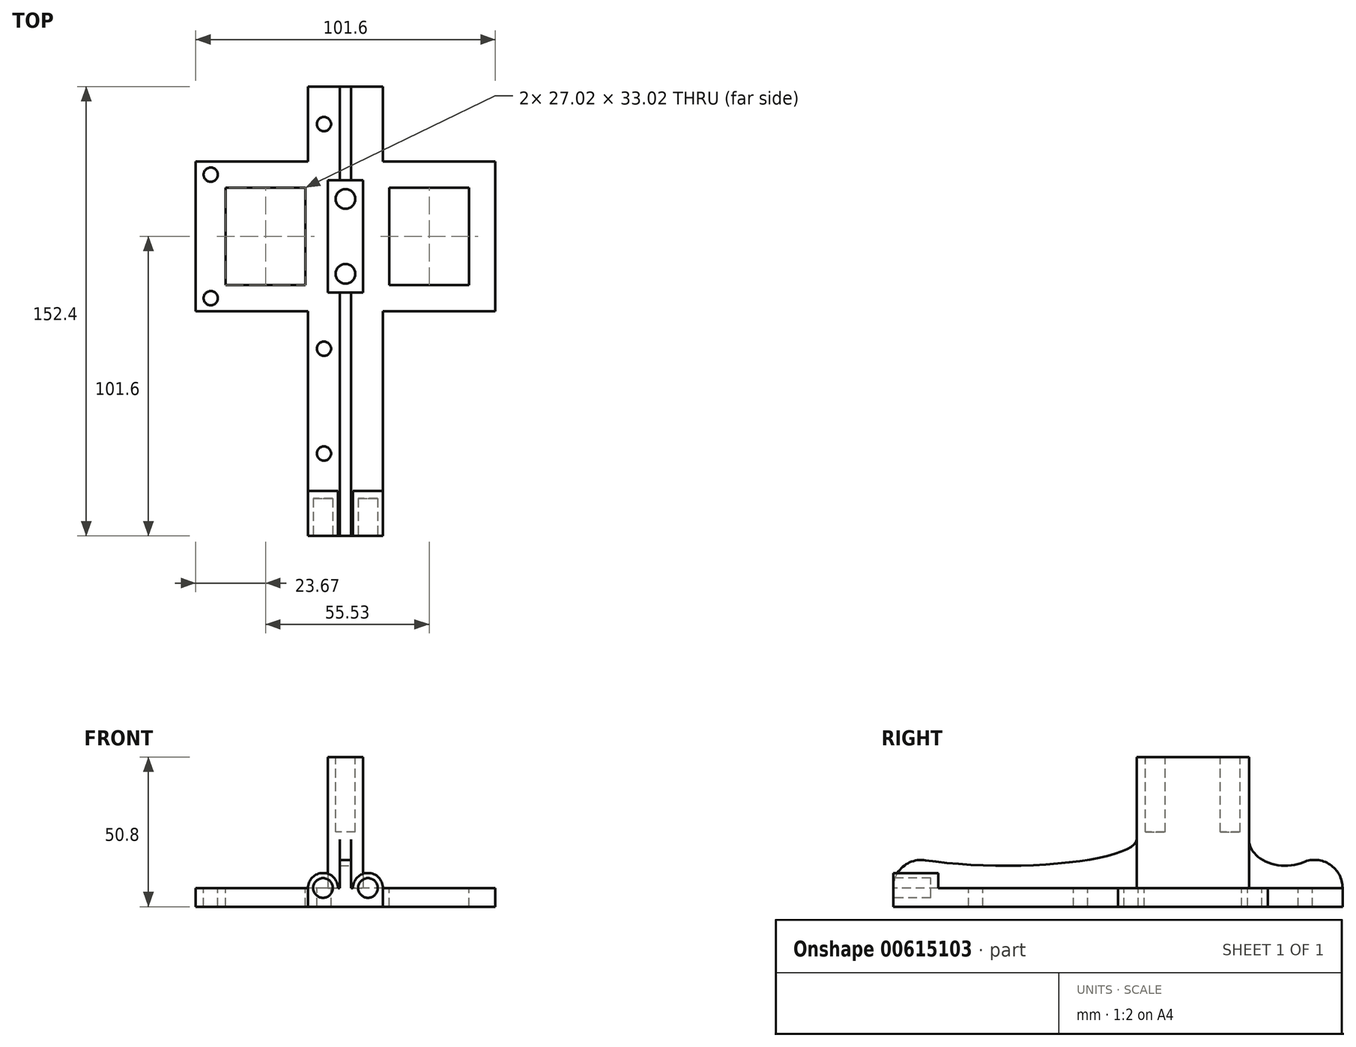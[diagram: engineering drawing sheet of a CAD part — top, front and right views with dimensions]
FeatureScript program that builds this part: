
annotation { "Feature Type Name" : "Feature", "Feature Type Description" : "" }
export const myFeature = defineFeature(function(context is Context, id is Id, definition is map)
    precondition{}
    {
        {
            var Q0;
            Q0=qCreatedBy(makeId("Top.planeOp"),FACE);
            var sketch = newSketch(context, id + "F0", { "sketchPlane" : qUnion([Q0])});
            skLineSegment(sketch, "E0.bottom", {"start": v(-6, 19.05) * mm, "end": v(6, 19.05) * mm});
            skLineSegment(sketch, "E0.top", {"start": v(-6, -19.05) * mm, "end": v(6, -19.05) * mm});
            skLineSegment(sketch, "E0.left", {"start": v(-6, 19.05) * mm, "end": v(-6, -19.05) * mm});
            skLineSegment(sketch, "E0.right", {"start": v(6, 19.05) * mm, "end": v(6, -19.05) * mm});
            skPoint(sketch, "E0.middle", {"position": v(0, 0) * mm});
            skSolve(sketch);
        }
        {
            var Q0;
            Q0 = qSketchRegion(id + "F0", true);
            extrude(context, id + "F1", {"entities" : qUnion([Q0]), "depth" : 50.8 * mm, "offsetDistance" : 25.4 * mm});
        }
        {
            var Q0;
            Q0=makeQuery(id+"F1.opExtrude","CAP_FACE",FACE,{"disambiguationData":[OSD([sQuery(id+"F0.wireOp",EDGE,"E0.bottom"),sQuery(id+"F0.wireOp",EDGE,"E0.top"),sQuery(id+"F0.wireOp",EDGE,"E0.left"),sQuery(id+"F0.wireOp",EDGE,"E0.right")])],"isStart":false});
            var sketch = newSketch(context, id + "F2", { "sketchPlane" : qUnion([Q0])});
            skCircle(sketch, "E1", {"center": v(0, 12.7) * mm, "radius": 3.33 * mm});
            skCircle(sketch, "E2", {"center": v(0, -12.7) * mm, "radius": 3.33 * mm});
            skSolve(sketch);
        }
        {
            var Q0;
            Q0 = qSketchRegion(id + "F2", true);
            extrude(context, id + "F3", {"entities" : qUnion([Q0]), "operationType" : NewBodyOperationType.REMOVE, "oppositeDirection" : true, "depth" : 25.4 * mm, "offsetDistance" : 25.4 * mm});
        }
        {
            var Q0;
            Q0=makeQuery(id+"F1.opExtrude","CAP_FACE",FACE,{"disambiguationData":[OSD([sQuery(id+"F0.wireOp",EDGE,"E0.bottom"),sQuery(id+"F0.wireOp",EDGE,"E0.top"),sQuery(id+"F0.wireOp",EDGE,"E0.left"),sQuery(id+"F0.wireOp",EDGE,"E0.right")])],"isStart":true});
            var sketch = newSketch(context, id + "F4", { "sketchPlane" : qUnion([Q0])});
            skLineSegment(sketch, "E3.0.0", {"start": v(-6, 19.05) * mm, "end": v(-6, -19.05) * mm});
            skLineSegment(sketch, "E3.0.1", {"start": v(-6, -19.05) * mm, "end": v(6, -19.05) * mm});
            skLineSegment(sketch, "E3.0.2", {"start": v(6, -19.05) * mm, "end": v(6, 19.05) * mm});
            skLineSegment(sketch, "E3.0.3", {"start": v(6, 19.05) * mm, "end": v(-6, 19.05) * mm});
            skLineSegment(sketch, "E4.bottom", {"start": v(12.7, 101.6) * mm, "end": v(-12.7, 101.6) * mm});
            skLineSegment(sketch, "E4.top", {"start": v(12.7, -50.8) * mm, "end": v(-12.7, -50.8) * mm});
            skLineSegment(sketch, "E4.left", {"start": v(12.7, 101.6) * mm, "end": v(12.7, -50.8) * mm});
            skLineSegment(sketch, "E4.right", {"start": v(-12.7, 101.6) * mm, "end": v(-12.7, -50.8) * mm});
            skPoint(sketch, "E4.middle", {"position": v(0, 25.4) * mm});
            skLineSegment(sketch, "E5.bottom", {"start": v(-50.8, 25.4) * mm, "end": v(50.8, 25.4) * mm});
            skLineSegment(sketch, "E5.top", {"start": v(-50.8, -25.4) * mm, "end": v(50.8, -25.4) * mm});
            skLineSegment(sketch, "E5.left", {"start": v(-50.8, 25.4) * mm, "end": v(-50.8, -25.4) * mm});
            skLineSegment(sketch, "E5.right", {"start": v(50.8, 25.4) * mm, "end": v(50.8, -25.4) * mm});
            skPoint(sketch, "E5.middle", {"position": v(0, 0) * mm});
            skLineSegment(sketch, "E6", {"start": v(0, 0) * mm, "end": v(0, 95.25) * mm, "construction": true});
            skSolve(sketch);
        }
        {
            var Q0;
            Q0 = qSketchRegion(id + "F4", true);
            extrude(context, id + "F5", {"entities" : qUnion([Q0]), "operationType" : NewBodyOperationType.ADD, "oppositeDirection" : true, "depth" : 6.35 * mm, "offsetDistance" : 25.4 * mm});
        }
        {
            var Q0;
            Q0=qCreatedBy(makeId("Right.planeOp"),FACE);
            var sketch = newSketch(context, id + "F6", { "sketchPlane" : qUnion([Q0])});
            skLineSegment(sketch, "E7.0", {"start": v(-19.05, 50.8) * mm, "end": v(-19.05, 6.35) * mm});
            skLineSegment(sketch, "E8.0", {"start": v(-101.6, 6.35) * mm, "end": v(-25.4, 6.35) * mm});
            skLineSegment(sketch, "E9.0", {"start": v(-25.4, 6.35) * mm, "end": v(25.4, 6.35) * mm});
            skEllipse(sketch, "E10", {"center": v(-63.5, 22.86) * mm, "majorRadius": 44.45 * mm, "minorRadius": 8.96 * mm, "majorAxis": v(1, 0), "construction": true});
            skCircle(sketch, "E11", {"center": v(-92.08, 6.35) * mm, "radius": 9.53 * mm, "construction": true});
            skLineSegment(sketch, "E12", {"start": v(-19.05, 22.86) * mm, "end": v(-19.05, 6.35) * mm});
            skArc(sketch, "E13", {"start": v(-101.6, 6.35) * mm, "mid": v(-98.27, 13.58) * mm, "end": v(-90.61, 15.76) * mm});
            skEllipse(sketch, "E14", {"center": v(-63.5, 22.86) * mm, "majorRadius": 44.45 * mm, "minorRadius": 8.96 * mm, "majorAxis": v(1, 0)});
            skLineSegment(sketch, "E15.0", {"start": v(25.4, 6.35) * mm, "end": v(50.8, 6.35) * mm});
            skLineSegment(sketch, "E16.0", {"start": v(19.05, 50.8) * mm, "end": v(19.05, 6.35) * mm});
            skArc(sketch, "E17", {"start": v(50.8, 6.35) * mm, "mid": v(46.53, 14.3) * mm, "end": v(37.56, 15.12) * mm});
            skEllipse(sketch, "E18", {"center": v(31.36, 22.86) * mm, "majorRadius": 12.31 * mm, "minorRadius": 8.96 * mm, "majorAxis": v(-1, 0)});
            skLineSegment(sketch, "E19", {"start": v(31.36, 13.9) * mm, "end": v(-63.5, 13.9) * mm, "construction": true});
            skSolve(sketch);
        }
        {
            var Q0;
            {var subQ3=sQuery(id+"F6.wireOp",EDGE,"E8.0");Q0=makeQuery(id+"F6.imprint","IMPRINT",FACE,{"disambiguationData":[TD([[makeQuery(id+"F6.imprint","IMPRINT",EDGE,{"derivedFrom":subQ3}),1.0]])]});}
            var Q1;
            {var subQ6=sQuery(id+"F6.wireOp",EDGE,"E15.0");Q1=makeQuery(id+"F6.imprint","IMPRINT",FACE,{"disambiguationData":[TD([[makeQuery(id+"F6.imprint","IMPRINT",EDGE,{"derivedFrom":subQ6}),1.0]])]});}
            extrude(context, id + "F7", {"entities" : qUnion([Q0, Q1]), "operationType" : NewBodyOperationType.ADD, "endBound" : BoundingType.SYMMETRIC, "depth" : 3.8 * mm, "offsetDistance" : 25.4 * mm});
        }
        {
            var Q0;
            Q0=makeQuery(id+"F5.opExtrude","SWEPT_FACE",FACE,{"disambiguationData":[OSD([sQuery(id+"F4.wireOp",EDGE,"E4.bottom")])]});
            var sketch = newSketch(context, id + "F8", { "sketchPlane" : qUnion([Q0])});
            skCircle(sketch, "E20", {"center": v(-7.62, 6.35) * mm, "radius": 3.33 * mm});
            skCircle(sketch, "E21", {"center": v(7.62, 6.35) * mm, "radius": 3.33 * mm});
            skSolve(sketch);
        }
        {
            var Q0;
            Q0 = qSketchRegion(id + "F8", true);
            extrude(context, id + "F9", {"entities" : qUnion([Q0]), "operationType" : NewBodyOperationType.REMOVE, "oppositeDirection" : true, "depth" : 12.7 * mm, "offsetDistance" : 25.4 * mm});
        }
        {
            var Q0;
            Q0=makeQuery(id+"F5.opExtrude","SWEPT_FACE",FACE,{"disambiguationData":[OSD([sQuery(id+"F4.wireOp",EDGE,"E4.bottom")])]});
            var sketch = newSketch(context, id + "F10", { "sketchPlane" : qUnion([Q0])});
            skArc(sketch, "E22.0", {"start": v(-10.95, 6.35) * mm, "mid": v(-7.62, 3.02) * mm, "end": v(-4.29, 6.35) * mm});
            skArc(sketch, "E23.0", {"start": v(4.29, 6.35) * mm, "mid": v(7.62, 3.02) * mm, "end": v(10.95, 6.35) * mm});
            skCircle(sketch, "E24", {"center": v(-7.62, 6.35) * mm, "radius": 5.08 * mm});
            skCircle(sketch, "E25", {"center": v(7.62, 6.35) * mm, "radius": 5.08 * mm});
            skCircle(sketch, "E26", {"center": v(-7.62, 6.35) * mm, "radius": 3.33 * mm});
            skCircle(sketch, "E27", {"center": v(7.62, 6.35) * mm, "radius": 3.33 * mm});
            skSolve(sketch);
        }
        {
            var Q0;
            Q0 = qSketchRegion(id + "F10", true);
            extrude(context, id + "F11", {"entities" : qUnion([Q0]), "operationType" : NewBodyOperationType.ADD, "oppositeDirection" : true, "depth" : 15.24 * mm, "offsetDistance" : 25.4 * mm});
        }
        {
            var Q0;
            Q0=makeQuery(id+"F11.opExtrude","CAP_FACE",FACE,{"disambiguationData":[OSD([sQuery(id+"F10.wireOp",EDGE,"E25"),sQuery(id+"F10.wireOp",EDGE,"E27")])],"isStart":false});
            var sketch = newSketch(context, id + "F12", { "sketchPlane" : qUnion([Q0])});
            skArc(sketch, "E28.0", {"start": v(-10.95, 6.35) * mm, "mid": v(-7.62, 9.68) * mm, "end": v(-4.29, 6.35) * mm});
            skArc(sketch, "E29.0", {"start": v(4.29, 6.35) * mm, "mid": v(7.62, 9.68) * mm, "end": v(10.95, 6.35) * mm});
            skLineSegment(sketch, "E30.0", {"start": v(4.29, 6.35) * mm, "end": v(10.95, 6.35) * mm});
            skLineSegment(sketch, "E31.0", {"start": v(-10.95, 6.35) * mm, "end": v(-4.29, 6.35) * mm});
            skSolve(sketch);
        }
        {
            var Q0;
            Q0 = qSketchRegion(id + "F12", true);
            extrude(context, id + "F13", {"entities" : qUnion([Q0]), "operationType" : NewBodyOperationType.ADD, "oppositeDirection" : true, "depth" : 2.54 * mm, "offsetDistance" : 25.4 * mm});
        }
        {
            var Q0;
            {var subQ0=sQuery(id+"F4.wireOp",EDGE,"E5.left");var subQ1=sQuery(id+"F4.wireOp",EDGE,"E5.top");var subQ2=sQuery(id+"F4.wireOp",EDGE,"E4.right");var subQ6=sQuery(id+"F4.wireOp",EDGE,"E5.bottom");var subQ8=sQuery(id+"F4.wireOp",EDGE,"E4.top");var subQ9=sQuery(id+"F4.wireOp",EDGE,"E4.bottom");Q0=makeQuery(id+"F7.boolean.opBoolean","SPLIT",FACE,{"disambiguationData":[TD([makeQuery(id+"F1.opExtrude","SWEPT_FACE",FACE,{"disambiguationData":[OSD([sQuery(id+"F0.wireOp",EDGE,"E0.left")])]})])],"derivedFrom":makeQuery(id+"F5.opExtrude","CAP_FACE",FACE,{"disambiguationData":[OSD([sQuery(id+"F4.wireOp",EDGE,"E3.0.0"),sQuery(id+"F4.wireOp",EDGE,"E3.0.1"),sQuery(id+"F4.wireOp",EDGE,"E3.0.2"),sQuery(id+"F4.wireOp",EDGE,"E3.0.3"),subQ9,subQ8,sQuery(id+"F4.wireOp",EDGE,"E4.left"),subQ2,subQ6,subQ1,subQ0,sQuery(id+"F4.wireOp",EDGE,"E5.right")])],"isStart":false})});}
            var sketch = newSketch(context, id + "F14", { "sketchPlane" : qUnion([Q0])});
            skLineSegment(sketch, "E32.0", {"start": v(-50.8, -25.4) * mm, "end": v(-50.8, 25.4) * mm});
            skLineSegment(sketch, "E33.0.0", {"start": v(-12.7, -86.36) * mm, "end": v(-2.54, -86.36) * mm});
            skLineSegment(sketch, "E33.0.1", {"start": v(-2.54, -86.36) * mm, "end": v(-2.54, -101.6) * mm});
            skLineSegment(sketch, "E33.0.2", {"start": v(-2.54, -101.6) * mm, "end": v(-1.9, -101.6) * mm});
            skLineSegment(sketch, "E33.0.3", {"start": v(-1.9, -101.6) * mm, "end": v(-1.9, -19.05) * mm});
            skLineSegment(sketch, "E33.0.4", {"start": v(-1.9, -19.05) * mm, "end": v(-6, -19.05) * mm});
            skLineSegment(sketch, "E33.0.5", {"start": v(-6, -19.05) * mm, "end": v(-6, 19.05) * mm});
            skLineSegment(sketch, "E33.0.6", {"start": v(-6, 19.05) * mm, "end": v(-1.9, 19.05) * mm});
            skLineSegment(sketch, "E33.0.7", {"start": v(-1.9, 19.05) * mm, "end": v(-1.9, 50.8) * mm});
            skLineSegment(sketch, "E33.0.8", {"start": v(-1.9, 50.8) * mm, "end": v(-12.7, 50.8) * mm});
            skLineSegment(sketch, "E33.0.9", {"start": v(-12.7, 50.8) * mm, "end": v(-12.7, 25.4) * mm});
            skLineSegment(sketch, "E33.0.10", {"start": v(-12.7, 25.4) * mm, "end": v(-50.8, 25.4) * mm});
            skLineSegment(sketch, "E33.0.11", {"start": v(-50.8, 25.4) * mm, "end": v(-50.8, -25.4) * mm});
            skLineSegment(sketch, "E33.0.12", {"start": v(-50.8, -25.4) * mm, "end": v(-12.7, -25.4) * mm});
            skLineSegment(sketch, "E33.0.13", {"start": v(-12.7, -25.4) * mm, "end": v(-12.7, -86.36) * mm});
            skLineSegment(sketch, "E34.0.0", {"start": v(2.54, -101.6) * mm, "end": v(2.54, -86.36) * mm});
            skLineSegment(sketch, "E34.0.1", {"start": v(2.54, -86.36) * mm, "end": v(12.7, -86.36) * mm});
            skLineSegment(sketch, "E34.0.2", {"start": v(12.7, -86.36) * mm, "end": v(12.7, -25.4) * mm});
            skLineSegment(sketch, "E34.0.3", {"start": v(12.7, -25.4) * mm, "end": v(50.8, -25.4) * mm});
            skLineSegment(sketch, "E34.0.4", {"start": v(50.8, -25.4) * mm, "end": v(50.8, 25.4) * mm});
            skLineSegment(sketch, "E34.0.5", {"start": v(50.8, 25.4) * mm, "end": v(12.7, 25.4) * mm});
            skLineSegment(sketch, "E34.0.6", {"start": v(12.7, 25.4) * mm, "end": v(12.7, 50.8) * mm});
            skLineSegment(sketch, "E34.0.7", {"start": v(12.7, 50.8) * mm, "end": v(1.9, 50.8) * mm});
            skLineSegment(sketch, "E34.0.8", {"start": v(1.9, 50.8) * mm, "end": v(1.9, 19.05) * mm});
            skLineSegment(sketch, "E34.0.9", {"start": v(1.9, 19.05) * mm, "end": v(6, 19.05) * mm});
            skLineSegment(sketch, "E34.0.10", {"start": v(6, 19.05) * mm, "end": v(6, -19.05) * mm});
            skLineSegment(sketch, "E34.0.11", {"start": v(6, -19.05) * mm, "end": v(1.9, -19.05) * mm});
            skLineSegment(sketch, "E34.0.12", {"start": v(1.9, -19.05) * mm, "end": v(1.9, -101.6) * mm});
            skLineSegment(sketch, "E34.0.13", {"start": v(1.9, -101.6) * mm, "end": v(2.54, -101.6) * mm});
            skLineSegment(sketch, "E35.bottom", {"start": v(-40.64, -16.5) * mm, "end": v(-13.62, -16.51) * mm});
            skLineSegment(sketch, "E35.top", {"start": v(-40.64, 16.51) * mm, "end": v(-13.62, 16.51) * mm});
            skLineSegment(sketch, "E35.left", {"start": v(-40.64, -16.5) * mm, "end": v(-40.64, 16.51) * mm});
            skLineSegment(sketch, "E35.right", {"start": v(-13.62, -16.51) * mm, "end": v(-13.62, 16.5) * mm});
            skPoint(sketch, "E35.middle", {"position": v(-27.13, 0) * mm});
            skLineSegment(sketch, "E36.bottom", {"start": v(41.91, -16.51) * mm, "end": v(14.89, -16.51) * mm});
            skLineSegment(sketch, "E36.top", {"start": v(41.91, 16.51) * mm, "end": v(14.89, 16.51) * mm});
            skLineSegment(sketch, "E36.left", {"start": v(41.91, -16.51) * mm, "end": v(41.91, 16.51) * mm});
            skLineSegment(sketch, "E36.right", {"start": v(14.89, -16.51) * mm, "end": v(14.89, 16.51) * mm});
            skPoint(sketch, "E36.middle", {"position": v(28.4, 0) * mm});
            skSolve(sketch);
        }
        {
            var Q0;
            Q0=makeQuery(id+"F14.imprint","IMPRINT",FACE,{"disambiguationData":[TD([[makeQuery(id+"F14.imprint","IMPRINT",EDGE,{"derivedFrom":sQuery(id+"F14.wireOp",EDGE,"E35.bottom")}),1.0]])]});
            var Q1;
            Q1=makeQuery(id+"F14.imprint","IMPRINT",FACE,{"disambiguationData":[TD([[makeQuery(id+"F14.imprint","IMPRINT",EDGE,{"derivedFrom":sQuery(id+"F14.wireOp",EDGE,"E36.bottom")}),-1.0]])]});
            extrude(context, id + "F15", {"entities" : qUnion([Q0, Q1]), "operationType" : NewBodyOperationType.REMOVE, "endBound" : BoundingType.THROUGH_ALL, "oppositeDirection" : true, "depth" : 25.4 * mm, "offsetDistance" : 25.4 * mm});
        }
        {
            var Q0;
            {var subQ0=sQuery(id+"F4.wireOp",EDGE,"E5.left");var subQ1=sQuery(id+"F4.wireOp",EDGE,"E5.top");var subQ2=sQuery(id+"F4.wireOp",EDGE,"E4.right");var subQ6=sQuery(id+"F4.wireOp",EDGE,"E5.bottom");var subQ8=sQuery(id+"F4.wireOp",EDGE,"E4.top");var subQ9=sQuery(id+"F4.wireOp",EDGE,"E4.bottom");Q0=makeQuery(id+"F7.boolean.opBoolean","SPLIT",FACE,{"disambiguationData":[TD([makeQuery(id+"F1.opExtrude","SWEPT_FACE",FACE,{"disambiguationData":[OSD([sQuery(id+"F0.wireOp",EDGE,"E0.left")])]})])],"derivedFrom":makeQuery(id+"F5.opExtrude","CAP_FACE",FACE,{"disambiguationData":[OSD([sQuery(id+"F4.wireOp",EDGE,"E3.0.0"),sQuery(id+"F4.wireOp",EDGE,"E3.0.1"),sQuery(id+"F4.wireOp",EDGE,"E3.0.2"),sQuery(id+"F4.wireOp",EDGE,"E3.0.3"),subQ9,subQ8,sQuery(id+"F4.wireOp",EDGE,"E4.left"),subQ2,subQ6,subQ1,subQ0,sQuery(id+"F4.wireOp",EDGE,"E5.right")])],"isStart":false})});}
            var sketch = newSketch(context, id + "F16", { "sketchPlane" : qUnion([Q0])});
            skCircle(sketch, "E37", {"center": v(-7.3, -73.66) * mm, "radius": 2.41 * mm});
            skCircle(sketch, "E38", {"center": v(-7.3, -38.1) * mm, "radius": 2.41 * mm});
            skCircle(sketch, "E39", {"center": v(-45.72, -20.96) * mm, "radius": 2.41 * mm});
            skCircle(sketch, "E40", {"center": v(-45.72, 20.96) * mm, "radius": 2.41 * mm});
            skCircle(sketch, "E41", {"center": v(-7.3, 38.1) * mm, "radius": 2.41 * mm});
            skLineSegment(sketch, "E42", {"start": v(-40.64, 16.51) * mm, "end": v(-50.8, 25.4) * mm, "construction": true});
            skLineSegment(sketch, "E43", {"start": v(-50.8, 25.4) * mm, "end": v(-50.8, -25.4) * mm, "construction": true});
            skLineSegment(sketch, "E44", {"start": v(-50.8, -25.4) * mm, "end": v(-40.64, -16.5) * mm, "construction": true});
            skSolve(sketch);
        }
        {
            var Q0;
            Q0 = qSketchRegion(id + "F16", true);
            extrude(context, id + "F17", {"entities" : qUnion([Q0]), "operationType" : NewBodyOperationType.REMOVE, "endBound" : BoundingType.THROUGH_ALL, "oppositeDirection" : true, "depth" : 25.4 * mm, "offsetDistance" : 25.4 * mm});
        }
    });
